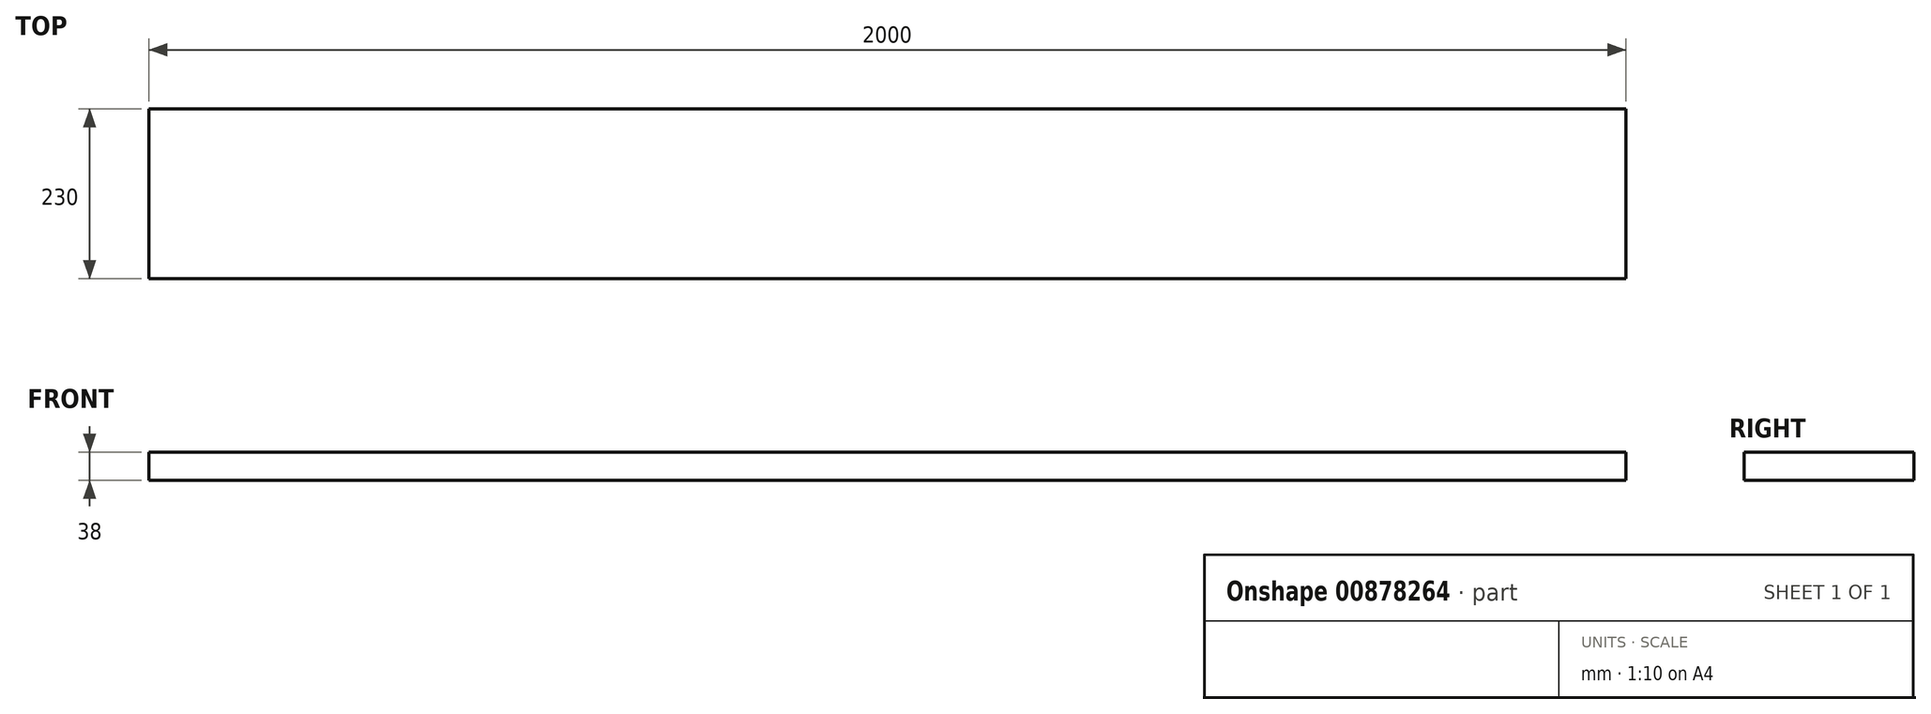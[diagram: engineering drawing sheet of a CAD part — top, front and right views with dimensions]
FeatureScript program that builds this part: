
annotation { "Feature Type Name" : "Feature", "Feature Type Description" : "" }
export const myFeature = defineFeature(function(context is Context, id is Id, definition is map)
    precondition{}
    {
        {
            var Q0;
            Q0=qCreatedBy(makeId("Top.planeOp"),FACE);
            var sketch = newSketch(context, id + "F0", { "sketchPlane" : qUnion([Q0])});
            skLineSegment(sketch, "E0.bottom", {"start": v(0, 0) * mm, "end": v(2000, 0) * mm});
            skLineSegment(sketch, "E0.top", {"start": v(0, 230) * mm, "end": v(2000, 230) * mm});
            skLineSegment(sketch, "E0.left", {"start": v(0, 0) * mm, "end": v(0, 230) * mm});
            skLineSegment(sketch, "E0.right", {"start": v(2000, 0) * mm, "end": v(2000, 230) * mm});
            skSolve(sketch);
        }
        {
            var Q0;
            Q0 = qSketchRegion(id + "F0", true);
            extrude(context, id + "F1", {"entities" : qUnion([Q0]), "depth" : 38 * mm, "offsetDistance" : 25 * mm});
        }
    });
